# Revit family: QF_Vivreau_PURITY C1000 AC
name_source: partatom
category: Specialty Equipment
units: mm (PartAtom-declared; Revit-internal decimal feet)

## family parameters
Always vertical = Yes
Cut with Voids When Loaded = No
OmniClass Number = 23.40.40.14.24
OmniClass Title = Food Dispensing Equipment
Part Type = Normal
Room Calculation Point = No
Round Connector Dimension = Use Diameter
Shared = No
Work Plane-Based = No

## types (1)
- QF_Vivreau_PURITY C1000 AC
    Assembly Code = E1090320
    CSI MasterFormat = 11 46 00
    Cold Water Connection Height = 0' - 9 1/2"
    Cold Water Flow = 0.617 GPM
    Cold Water Maximum Pressure = 125.00 psi
    Cold Water Minimum Pressure = 29.00 psi
    Cold Water RI Height = 0' - 0"
    Cold Water Size = 1"
    Cold Water Temperature Recommended = 40 °F
    Depth = 0' - 4 1/4"
    Description = Water Filter
    Foodservice Equipment Identifier = Yes
    Height = 0' - 9 3/8"
    Identify Quantity as Lot = Yes
    Manufacturer = Vivreau
    Masterspec = Division 11
    Model = PURITY C1000 AC
    Plumbing Connection Type = NPT
    Specification by Manufacturer = PURITY C1000 AC water filtration cartridge. Max. operating pressure 125 psi, water intake temperature 39.2 - 86 Fahrenheit. Dimensions with filter head  w/d/h 4.29/3.66/9.37 inch. Weight dry/wet 1.1/2.2 lb, position vertical. 2 step filtration process with pre-filtration and activated carbon filtration.
    URL = www.vivreauwater.com/professional-filters
    URL Cutsheet = https://vivreauwater.com
    Weight in Pounds = 2.2
    Width = 0' - 4 1/4"

## geometry (parser evidence)
native form markers: Sweep x10
no freeform markers — native parametric forms only
